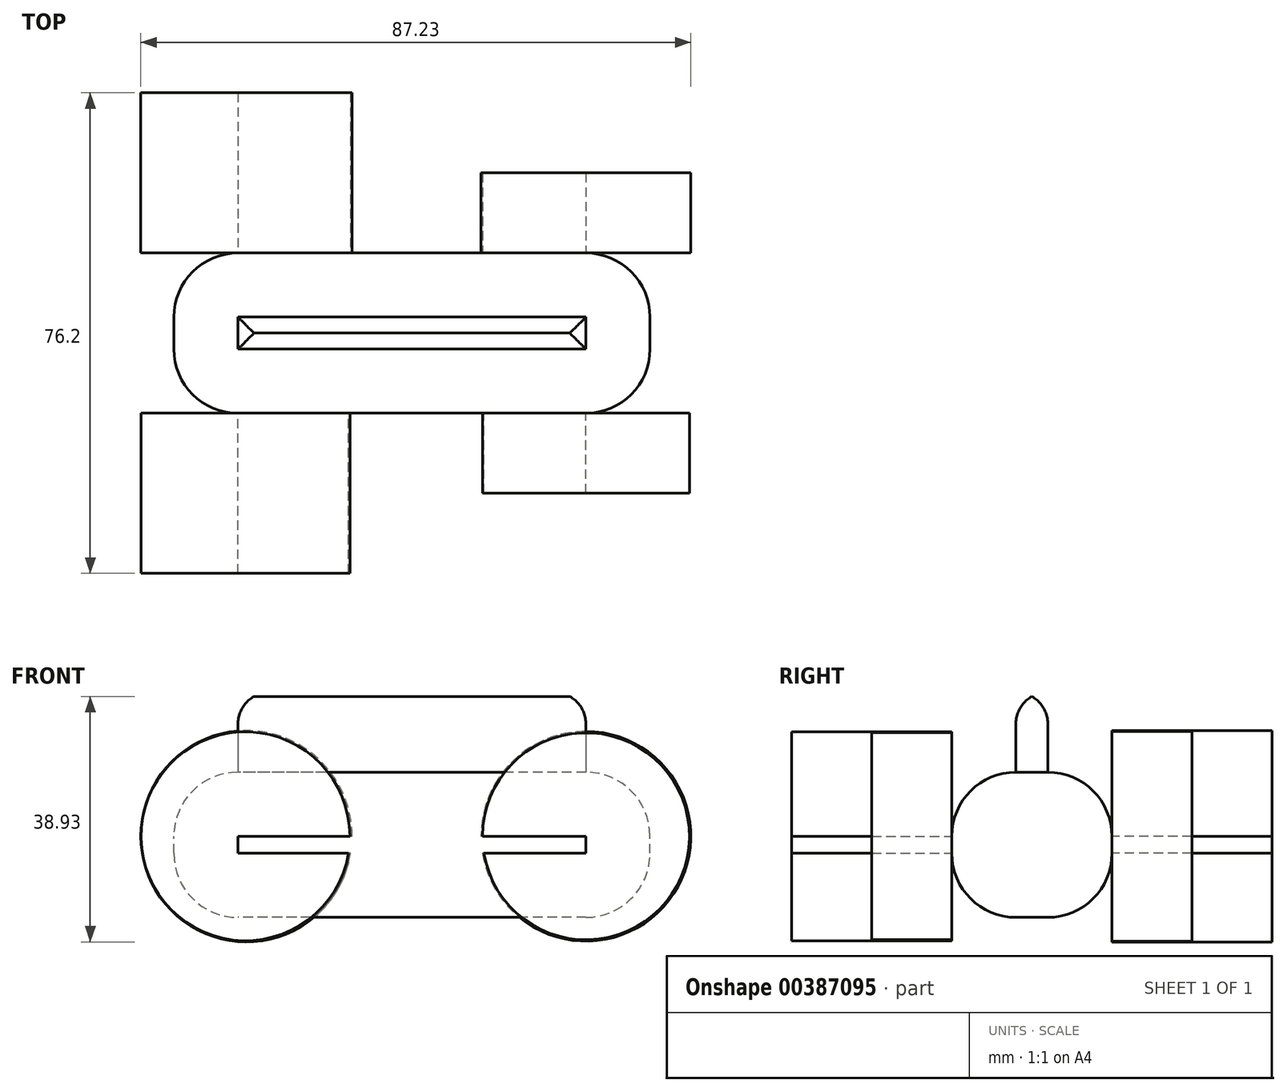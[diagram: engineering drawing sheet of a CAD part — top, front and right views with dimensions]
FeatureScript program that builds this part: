
annotation { "Feature Type Name" : "Feature", "Feature Type Description" : "" }
export const myFeature = defineFeature(function(context is Context, id is Id, definition is map)
    precondition{}
    {
        {
            var Q0;
            Q0=qCreatedBy(makeId("Front.planeOp"),FACE);
            var sketch = newSketch(context, id + "F0", { "sketchPlane" : qUnion([Q0])});
            skLineSegment(sketch, "E0.bottom", {"start": v(0, 0) * mm, "end": v(-75.52, 0) * mm});
            skLineSegment(sketch, "E0.top", {"start": v(0, 23.02) * mm, "end": v(-75.52, 23.02) * mm});
            skLineSegment(sketch, "E0.left", {"start": v(0, 0) * mm, "end": v(0, 23.02) * mm});
            skLineSegment(sketch, "E0.right", {"start": v(-75.52, 0) * mm, "end": v(-75.52, 23.02) * mm});
            skSolve(sketch);
        }
        {
            var Q0;
            Q0=makeQuery(id+"F0.imprint","IMPRINT",FACE,{"disambiguationData":[TD([[makeQuery(id+"F0.imprint","IMPRINT",EDGE,{"derivedFrom":sQuery(id+"F0.wireOp",EDGE,"E0.bottom")}),-1.0]])]});
            extrude(context, id + "F1", {"entities" : qUnion([Q0]), "depth" : 25.4 * mm});
        }
        {
            var Q0;
            Q0=makeQuery(id+"F1.opExtrude","CAP_EDGE",EDGE,{"disambiguationData":[OSD([sQuery(id+"F0.wireOp",EDGE,"E0.bottom")])],"isStart":false});
            var Q1;
            Q1=makeQuery(id+"F1.opExtrude","SWEPT_FACE",FACE,{"disambiguationData":[OSD([sQuery(id+"F0.wireOp",EDGE,"E0.right")])]});
            var Q2;
            Q2=makeQuery(id+"F1.opExtrude","CAP_FACE",FACE,{"disambiguationData":[OSD([sQuery(id+"F0.wireOp",EDGE,"E0.bottom"),sQuery(id+"F0.wireOp",EDGE,"E0.top"),sQuery(id+"F0.wireOp",EDGE,"E0.left"),sQuery(id+"F0.wireOp",EDGE,"E0.right")])],"isStart":true});
            var Q3;
            Q3=makeQuery(id+"F1.opExtrude","SWEPT_FACE",FACE,{"disambiguationData":[OSD([sQuery(id+"F0.wireOp",EDGE,"E0.top")])]});
            var Q4;
            Q4=makeQuery(id+"F1.opExtrude","SWEPT_FACE",FACE,{"disambiguationData":[OSD([sQuery(id+"F0.wireOp",EDGE,"E0.bottom")])]});
            var Q5;
            Q5=makeQuery(id+"F1.opExtrude","SWEPT_FACE",FACE,{"disambiguationData":[OSD([sQuery(id+"F0.wireOp",EDGE,"E0.left")])]});
            fillet(context, id + "F2", {"entities" : qUnion([Q0, Q1, Q2, Q3, Q4, Q5]), "radius" : 10.16 * mm, "tangentPropagation" : true, "allowEdgeOverflow" : false});
        }
        {
            var Q0;
            Q0=makeQuery(id+"F1.opExtrude","CAP_FACE",FACE,{"disambiguationData":[OSD([sQuery(id+"F0.wireOp",EDGE,"E0.bottom"),sQuery(id+"F0.wireOp",EDGE,"E0.top"),sQuery(id+"F0.wireOp",EDGE,"E0.left"),sQuery(id+"F0.wireOp",EDGE,"E0.right")])],"isStart":true});
            var sketch = newSketch(context, id + "F3", { "sketchPlane" : qUnion([Q0])});
            skCircle(sketch, "E1", {"center": v(64.01, 12.86) * mm, "radius": 16.75 * mm});
            skCircle(sketch, "E2", {"center": v(10.16, 12.86) * mm, "radius": 16.63 * mm});
            skSolve(sketch);
        }
        {
            var Q0;
            Q0=makeQuery(id+"F1.opExtrude","CAP_FACE",FACE,{"disambiguationData":[OSD([sQuery(id+"F0.wireOp",EDGE,"E0.bottom"),sQuery(id+"F0.wireOp",EDGE,"E0.top"),sQuery(id+"F0.wireOp",EDGE,"E0.left"),sQuery(id+"F0.wireOp",EDGE,"E0.right")])],"isStart":false});
            var sketch = newSketch(context, id + "F4", { "sketchPlane" : qUnion([Q0])});
            skCircle(sketch, "E3", {"center": v(-64.16, 12.86) * mm, "radius": 16.56 * mm});
            skCircle(sketch, "E4", {"center": v(-10.16, 12.86) * mm, "radius": 16.4 * mm});
            skSolve(sketch);
        }
        {
            var Q0;
            {var subQ1=sQuery(id+"F0.wireOp",EDGE,"E0.right");var subQ2=sQuery(id+"F0.wireOp",EDGE,"E0.top");var subQ3=sQuery(id+"F0.wireOp",EDGE,"E0.bottom");var subQ4=makeQuery(id+"F1.opExtrude","CAP_FACE",FACE,{"disambiguationData":[OSD([subQ3,subQ2,sQuery(id+"F0.wireOp",EDGE,"E0.left"),subQ1])],"isStart":false});var subQ9=makeQuery(id+"F2.opFillet","BLEND_EDGE",EDGE,{"blendedFrom":[makeQuery(id+"F1.opExtrude","CAP_EDGE",EDGE,{"disambiguationData":[OSD([subQ1])],"isStart":false}),subQ4],"blendedInto":[subQ4]});Q0=makeQuery(id+"F4.imprint","IMPRINT",FACE,{"disambiguationData":[TD([[makeQuery(id+"F4.imprint","IMPRINT",EDGE,{"derivedFrom":subQ9}),-1.0]])]});}
            extrude(context, id + "F5", {"entities" : qUnion([Q0]), "depth" : 25.4 * mm});
        }
        {
            var Q0;
            {var subQ1=sQuery(id+"F0.wireOp",EDGE,"E0.right");var subQ2=sQuery(id+"F0.wireOp",EDGE,"E0.top");var subQ3=sQuery(id+"F0.wireOp",EDGE,"E0.bottom");var subQ4=makeQuery(id+"F1.opExtrude","CAP_FACE",FACE,{"disambiguationData":[OSD([subQ3,subQ2,sQuery(id+"F0.wireOp",EDGE,"E0.left"),subQ1])],"isStart":true});var subQ9=makeQuery(id+"F2.opFillet","BLEND_EDGE",EDGE,{"blendedFrom":[makeQuery(id+"F1.opExtrude","CAP_EDGE",EDGE,{"disambiguationData":[OSD([subQ1])],"isStart":true}),subQ4],"blendedInto":[subQ4]});Q0=makeQuery(id+"F3.imprint","IMPRINT",FACE,{"disambiguationData":[TD([[makeQuery(id+"F3.imprint","IMPRINT",EDGE,{"derivedFrom":subQ9}),-1.0]])]});}
            extrude(context, id + "F6", {"entities" : qUnion([Q0]), "depth" : 25.4 * mm});
        }
        {
            var Q0;
            {var subQ1=sQuery(id+"F0.wireOp",EDGE,"E0.left");var subQ2=sQuery(id+"F0.wireOp",EDGE,"E0.top");var subQ3=sQuery(id+"F0.wireOp",EDGE,"E0.bottom");var subQ4=makeQuery(id+"F1.opExtrude","CAP_FACE",FACE,{"disambiguationData":[OSD([subQ3,subQ2,subQ1,sQuery(id+"F0.wireOp",EDGE,"E0.right")])],"isStart":false});var subQ9=makeQuery(id+"F2.opFillet","BLEND_EDGE",EDGE,{"blendedFrom":[makeQuery(id+"F1.opExtrude","CAP_EDGE",EDGE,{"disambiguationData":[OSD([subQ1])],"isStart":false}),subQ4],"blendedInto":[subQ4]});Q0=makeQuery(id+"F4.imprint","IMPRINT",FACE,{"disambiguationData":[TD([[makeQuery(id+"F4.imprint","IMPRINT",EDGE,{"derivedFrom":subQ9}),-1.0]])]});}
            extrude(context, id + "F7", {"entities" : qUnion([Q0]), "depth" : 12.7 * mm});
        }
        {
            var Q0;
            {var subQ1=sQuery(id+"F0.wireOp",EDGE,"E0.left");var subQ2=sQuery(id+"F0.wireOp",EDGE,"E0.top");var subQ3=sQuery(id+"F0.wireOp",EDGE,"E0.bottom");var subQ4=makeQuery(id+"F1.opExtrude","CAP_FACE",FACE,{"disambiguationData":[OSD([subQ3,subQ2,subQ1,sQuery(id+"F0.wireOp",EDGE,"E0.right")])],"isStart":true});var subQ9=makeQuery(id+"F2.opFillet","BLEND_EDGE",EDGE,{"blendedFrom":[makeQuery(id+"F1.opExtrude","CAP_EDGE",EDGE,{"disambiguationData":[OSD([subQ1])],"isStart":true}),subQ4],"blendedInto":[subQ4]});Q0=makeQuery(id+"F3.imprint","IMPRINT",FACE,{"disambiguationData":[TD([[makeQuery(id+"F3.imprint","IMPRINT",EDGE,{"derivedFrom":subQ9}),-1.0]])]});}
            extrude(context, id + "F8", {"entities" : qUnion([Q0]), "depth" : 12.7 * mm});
        }
        {
            var Q0;
            Q0=makeQuery(id+"F1.opExtrude","SWEPT_FACE",FACE,{"disambiguationData":[OSD([sQuery(id+"F0.wireOp",EDGE,"E0.top")])]});
            var sketch = newSketch(context, id + "F9", { "sketchPlane" : qUnion([Q0])});
            skLineSegment(sketch, "E5.bottom", {"start": v(-65.36, -15.24) * mm, "end": v(-10.16, -15.24) * mm});
            skLineSegment(sketch, "E5.top", {"start": v(-65.36, -10.16) * mm, "end": v(-10.16, -10.16) * mm});
            skLineSegment(sketch, "E5.left", {"start": v(-65.36, -15.24) * mm, "end": v(-65.36, -10.16) * mm});
            skLineSegment(sketch, "E5.right", {"start": v(-10.16, -15.24) * mm, "end": v(-10.16, -10.16) * mm});
            skSolve(sketch);
        }
        {
            var Q0;
            Q0 = qSketchRegion(id + "F9", true);
            extrude(context, id + "F10", {"entities" : qUnion([Q0]), "operationType" : NewBodyOperationType.ADD, "depth" : 12.7 * mm});
        }
        {
            var Q0;
            Q0=makeQuery(id+"F10.opExtrude","CAP_EDGE",EDGE,{"disambiguationData":[OSD([sQuery(id+"F9.wireOp",EDGE,"E5.right")])],"isStart":false});
            var Q1;
            Q1=makeQuery(id+"F10.opExtrude","CAP_EDGE",EDGE,{"disambiguationData":[OSD([sQuery(id+"F9.wireOp",EDGE,"E5.left")])],"isStart":false});
            var Q2;
            Q2=makeQuery(id+"F10.opExtrude","CAP_EDGE",EDGE,{"disambiguationData":[OSD([sQuery(id+"F9.wireOp",EDGE,"E5.top")])],"isStart":false});
            var Q3;
            Q3=makeQuery(id+"F10.opExtrude","CAP_EDGE",EDGE,{"disambiguationData":[OSD([sQuery(id+"F9.wireOp",EDGE,"E5.bottom")])],"isStart":false});
            fillet(context, id + "F11", {"entities" : qUnion([Q0, Q1, Q2, Q3]), "radius" : 5.08 * mm, "tangentPropagation" : true, "allowEdgeOverflow" : false});
        }
    });
